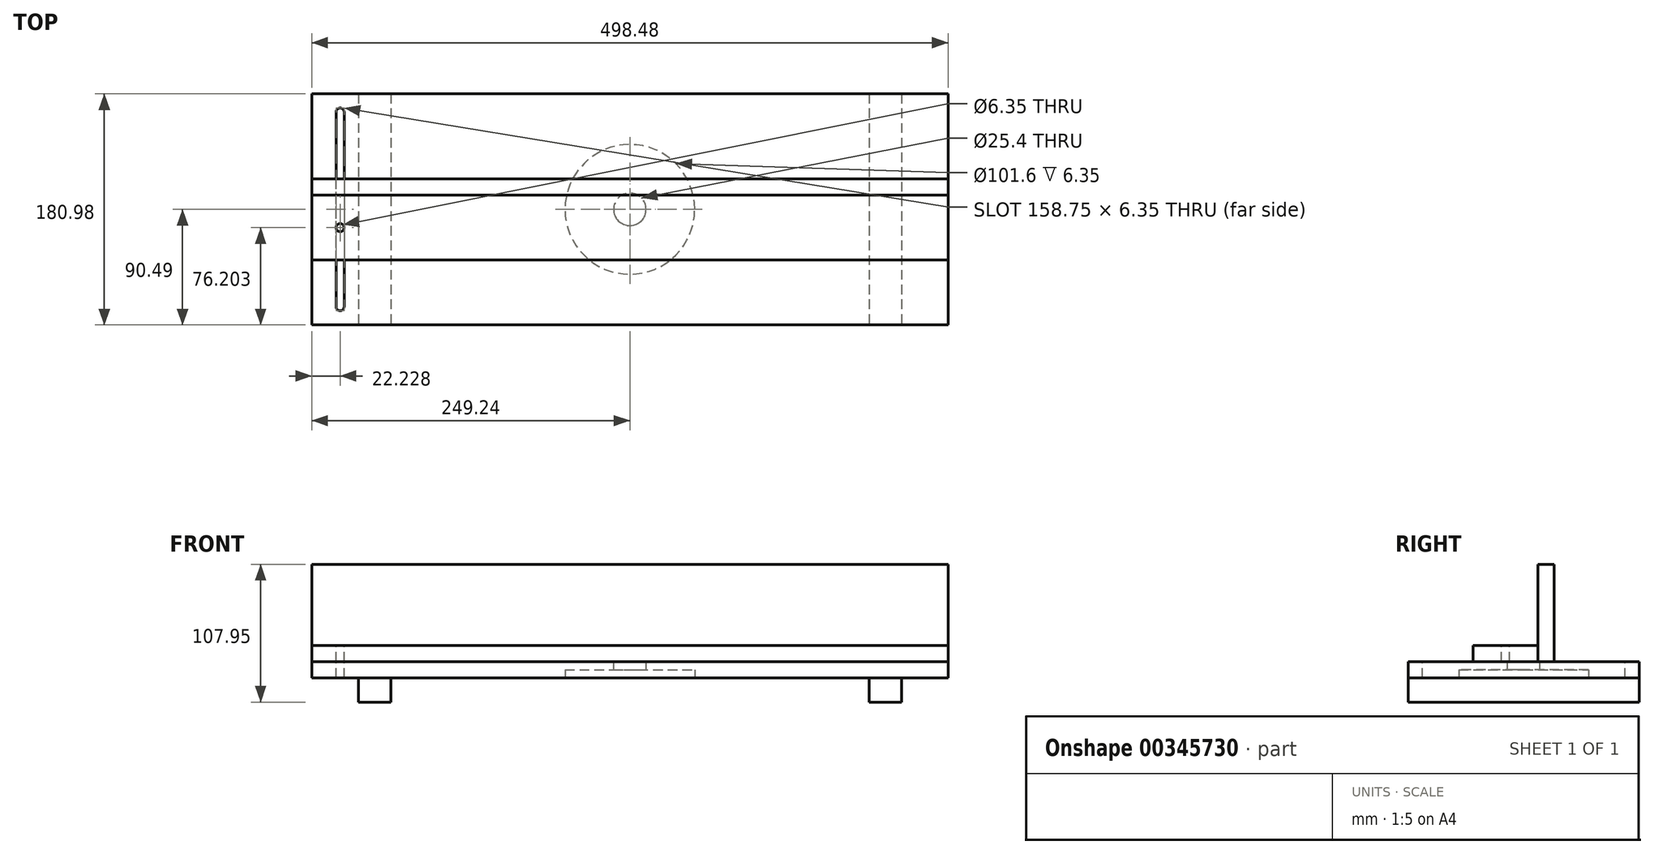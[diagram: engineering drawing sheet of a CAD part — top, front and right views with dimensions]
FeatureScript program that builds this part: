
annotation { "Feature Type Name" : "Feature", "Feature Type Description" : "" }
export const myFeature = defineFeature(function(context is Context, id is Id, definition is map)
    precondition{}
    {
        {
            var Q0;
            Q0=qCreatedBy(makeId("Top.planeOp"),FACE);
            var sketch = newSketch(context, id + "F0", { "sketchPlane" : qUnion([Q0])});
            skLineSegment(sketch, "E0.bottom", {"start": v(-249.24, 90.49) * mm, "end": v(249.24, 90.49) * mm});
            skLineSegment(sketch, "E0.top", {"start": v(-249.24, -90.49) * mm, "end": v(249.24, -90.49) * mm});
            skLineSegment(sketch, "E0.left", {"start": v(-249.24, 90.49) * mm, "end": v(-249.24, -90.49) * mm});
            skLineSegment(sketch, "E0.right", {"start": v(249.24, 90.49) * mm, "end": v(249.24, -90.49) * mm});
            skSolve(sketch);
        }
        {
            var Q0;
            Q0 = qSketchRegion(id + "F0", true);
            extrude(context, id + "F1", {"entities" : qUnion([Q0]), "depth" : 12.7 * mm});
        }
        {
            var Q0;
            Q0=makeQuery(id+"F1.opExtrude","SWEPT_FACE",FACE,{"disambiguationData":[OSD([sQuery(id+"F0.wireOp",EDGE,"E0.top")])]});
            var sketch = newSketch(context, id + "F2", { "sketchPlane" : qUnion([Q0])});
            skLineSegment(sketch, "E1.bottom", {"start": v(-212.73, 0) * mm, "end": v(-187.33, 0) * mm});
            skLineSegment(sketch, "E1.top", {"start": v(-212.73, -19.05) * mm, "end": v(-187.33, -19.05) * mm});
            skLineSegment(sketch, "E1.left", {"start": v(-212.73, 0) * mm, "end": v(-212.73, -19.05) * mm});
            skLineSegment(sketch, "E1.right", {"start": v(-187.33, 0) * mm, "end": v(-187.33, -19.05) * mm});
            skSolve(sketch);
        }
        {
            var Q0;
            Q0 = qSketchRegion(id + "F2", true);
            var Q1;
            Q1=makeQuery(id+"F1.opExtrude","SWEPT_FACE",FACE,{"disambiguationData":[OSD([sQuery(id+"F0.wireOp",EDGE,"E0.bottom")])]});
            extrude(context, id + "F3", {"entities" : qUnion([Q0]), "endBound" : BoundingType.UP_TO_SURFACE, "oppositeDirection" : true, "endBoundEntityFace" : qUnion([Q1]), "depth" : 304.8 * mm});
        }
        {
            var Q0;
            Q0=makeQuery(id+"F3.opExtrude","SWEPT_BODY",BODY,{"disambiguationData":[OSD([sQuery(id+"F2.wireOp",EDGE,"E1.bottom"),sQuery(id+"F2.wireOp",EDGE,"E1.top"),sQuery(id+"F2.wireOp",EDGE,"E1.left"),sQuery(id+"F2.wireOp",EDGE,"E1.right")])]});
            var Q1;
            Q1=qCreatedBy(makeId("Right.planeOp"),FACE);
            mirror(context, id + "F4", {"entities" : qUnion([Q0]), "mirrorPlane" : qUnion([Q1])});
        }
        {
            var Q0;
            Q0=makeQuery(id+"F1.opExtrude","CAP_FACE",FACE,{"disambiguationData":[OSD([sQuery(id+"F0.wireOp",EDGE,"E0.bottom"),sQuery(id+"F0.wireOp",EDGE,"E0.top"),sQuery(id+"F0.wireOp",EDGE,"E0.left"),sQuery(id+"F0.wireOp",EDGE,"E0.right")])],"isStart":false});
            var sketch = newSketch(context, id + "F5", { "sketchPlane" : qUnion([Q0])});
            skCircle(sketch, "E2", {"center": v(0, 0) * mm, "radius": 12.7 * mm});
            skSolve(sketch);
        }
        {
            var Q0;
            Q0 = qSketchRegion(id + "F5", true);
            extrude(context, id + "F6", {"entities" : qUnion([Q0]), "operationType" : NewBodyOperationType.REMOVE, "oppositeDirection" : true, "depth" : 25.4 * mm});
        }
        {
            var Q0;
            Q0=makeQuery(id+"F1.opExtrude","CAP_FACE",FACE,{"disambiguationData":[OSD([sQuery(id+"F0.wireOp",EDGE,"E0.bottom"),sQuery(id+"F0.wireOp",EDGE,"E0.top"),sQuery(id+"F0.wireOp",EDGE,"E0.left"),sQuery(id+"F0.wireOp",EDGE,"E0.right")])],"isStart":true});
            var sketch = newSketch(context, id + "F7", { "sketchPlane" : qUnion([Q0])});
            skCircle(sketch, "E3", {"center": v(0, 0) * mm, "radius": 50.8 * mm});
            skSolve(sketch);
        }
        {
            var Q0;
            Q0 = qSketchRegion(id + "F7", true);
            extrude(context, id + "F8", {"entities" : qUnion([Q0]), "operationType" : NewBodyOperationType.REMOVE, "oppositeDirection" : true, "depth" : 6.35 * mm});
        }
        {
            var Q0;
            Q0=makeQuery(id+"F1.opExtrude","CAP_FACE",FACE,{"disambiguationData":[OSD([sQuery(id+"F0.wireOp",EDGE,"E0.bottom"),sQuery(id+"F0.wireOp",EDGE,"E0.top"),sQuery(id+"F0.wireOp",EDGE,"E0.left"),sQuery(id+"F0.wireOp",EDGE,"E0.right")])],"isStart":false});
            var sketch = newSketch(context, id + "F9", { "sketchPlane" : qUnion([Q0])});
            skLineSegment(sketch, "E4", {"start": v(-230.19, -76.2) * mm, "end": v(-230.19, 76.2) * mm});
            skLineSegment(sketch, "E5", {"start": v(-223.84, 76.2) * mm, "end": v(-223.84, -76.2) * mm});
            skArc(sketch, "E6", {"start": v(-230.19, 76.2) * mm, "mid": v(-227.01, 79.38) * mm, "end": v(-223.84, 76.2) * mm});
            skArc(sketch, "E7", {"start": v(-230.19, -76.2) * mm, "mid": v(-227.01, -79.38) * mm, "end": v(-223.84, -76.2) * mm});
            skSolve(sketch);
        }
        {
            var Q0;
            Q0 = qSketchRegion(id + "F9", true);
            extrude(context, id + "F10", {"entities" : qUnion([Q0]), "operationType" : NewBodyOperationType.REMOVE, "oppositeDirection" : true, "depth" : 25.4 * mm});
        }
        {
            var Q0;
            Q0=qCreatedBy(makeId("Right.planeOp"),FACE);
            var sketch = newSketch(context, id + "F11", { "sketchPlane" : qUnion([Q0])});
            skLineSegment(sketch, "E8.bottom", {"start": v(-39.69, 25.4) * mm, "end": v(11.11, 25.4) * mm});
            skLineSegment(sketch, "E8.top", {"start": v(-39.69, 12.7) * mm, "end": v(11.11, 12.7) * mm});
            skLineSegment(sketch, "E8.left", {"start": v(-39.69, 25.4) * mm, "end": v(-39.69, 12.7) * mm});
            skLineSegment(sketch, "E8.right", {"start": v(11.11, 25.4) * mm, "end": v(11.11, 12.7) * mm});
            skSolve(sketch);
        }
        {
            var Q0;
            Q0 = qSketchRegion(id + "F11", true);
            extrude(context, id + "F12", {"entities" : qUnion([Q0]), "endBound" : BoundingType.SYMMETRIC, "depth" : 498.47 * mm});
        }
        {
            var Q0;
            Q0=makeQuery(id+"F12.opExtrude","SWEPT_FACE",FACE,{"disambiguationData":[OSD([sQuery(id+"F11.wireOp",EDGE,"E8.bottom")])]});
            var sketch = newSketch(context, id + "F13", { "sketchPlane" : qUnion([Q0])});
            skCircle(sketch, "E9", {"center": v(-227.01, -14.29) * mm, "radius": 3.18 * mm});
            skSolve(sketch);
        }
        {
            var Q0;
            Q0 = qSketchRegion(id + "F13", true);
            extrude(context, id + "F14", {"entities" : qUnion([Q0]), "operationType" : NewBodyOperationType.REMOVE, "oppositeDirection" : true, "depth" : 25.4 * mm});
        }
        {
            var Q0;
            Q0=qCreatedBy(makeId("Right.planeOp"),FACE);
            var sketch = newSketch(context, id + "F15", { "sketchPlane" : qUnion([Q0])});
            skLineSegment(sketch, "E10.bottom", {"start": v(11.11, 88.9) * mm, "end": v(23.81, 88.9) * mm});
            skLineSegment(sketch, "E10.top", {"start": v(11.11, 12.7) * mm, "end": v(23.81, 12.7) * mm});
            skLineSegment(sketch, "E10.left", {"start": v(11.11, 88.9) * mm, "end": v(11.11, 12.7) * mm});
            skLineSegment(sketch, "E10.right", {"start": v(23.81, 88.9) * mm, "end": v(23.81, 12.7) * mm});
            skSolve(sketch);
        }
        {
            var Q0;
            Q0 = qSketchRegion(id + "F15", true);
            extrude(context, id + "F16", {"entities" : qUnion([Q0]), "endBound" : BoundingType.SYMMETRIC, "depth" : 498.47 * mm});
        }
    });
